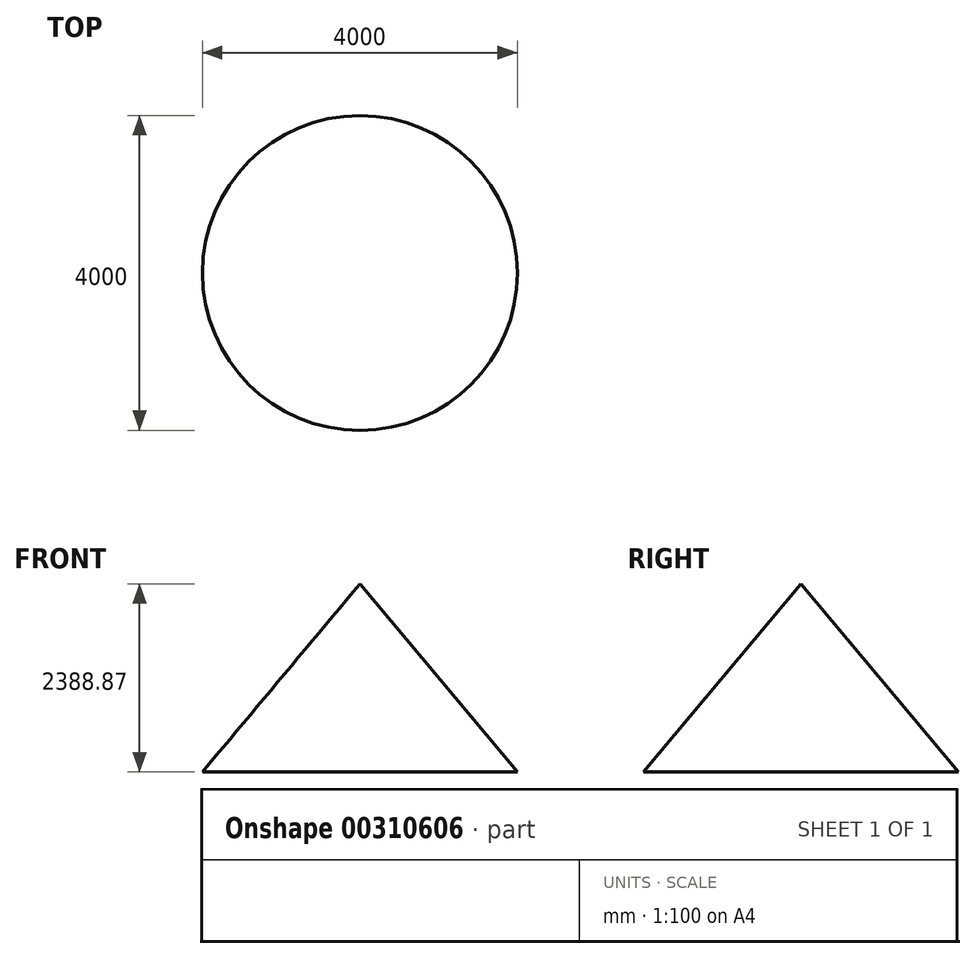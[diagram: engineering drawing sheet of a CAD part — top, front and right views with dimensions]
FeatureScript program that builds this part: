
annotation { "Feature Type Name" : "Feature", "Feature Type Description" : "" }
export const myFeature = defineFeature(function(context is Context, id is Id, definition is map)
    precondition{}
    {
        {
            var Q0;
            Q0=qCreatedBy(makeId("Front.planeOp"),FACE);
            var sketch = newSketch(context, id + "F0", { "sketchPlane" : qUnion([Q0])});
            skLineSegment(sketch, "E0", {"start": v(-993.9, 1743.95) * mm, "end": v(-993.9, -644.92) * mm});
            skLineSegment(sketch, "E1", {"start": v(-993.9, -644.92) * mm, "end": v(1006.1, -644.92) * mm});
            skLineSegment(sketch, "E2", {"start": v(-993.9, 1743.95) * mm, "end": v(1006.1, -644.92) * mm});
            skLineSegment(sketch, "E3", {"start": v(-993.9, 1743.95) * mm, "end": v(-993.9, -1772.5) * mm, "construction": true});
            skSolve(sketch);
        }
        {
            var Q0;
            Q0 = qSketchRegion(id + "F0", true);
            var Q1;
            Q1=sQuery(id+"F0.wireOp",EDGE,"E3");
            revolve(context, id + "F1", {"entities" : qUnion([Q0]), "axis" : qUnion([Q1]), "revolveType" : RevolveType.FULL});
        }
    });
